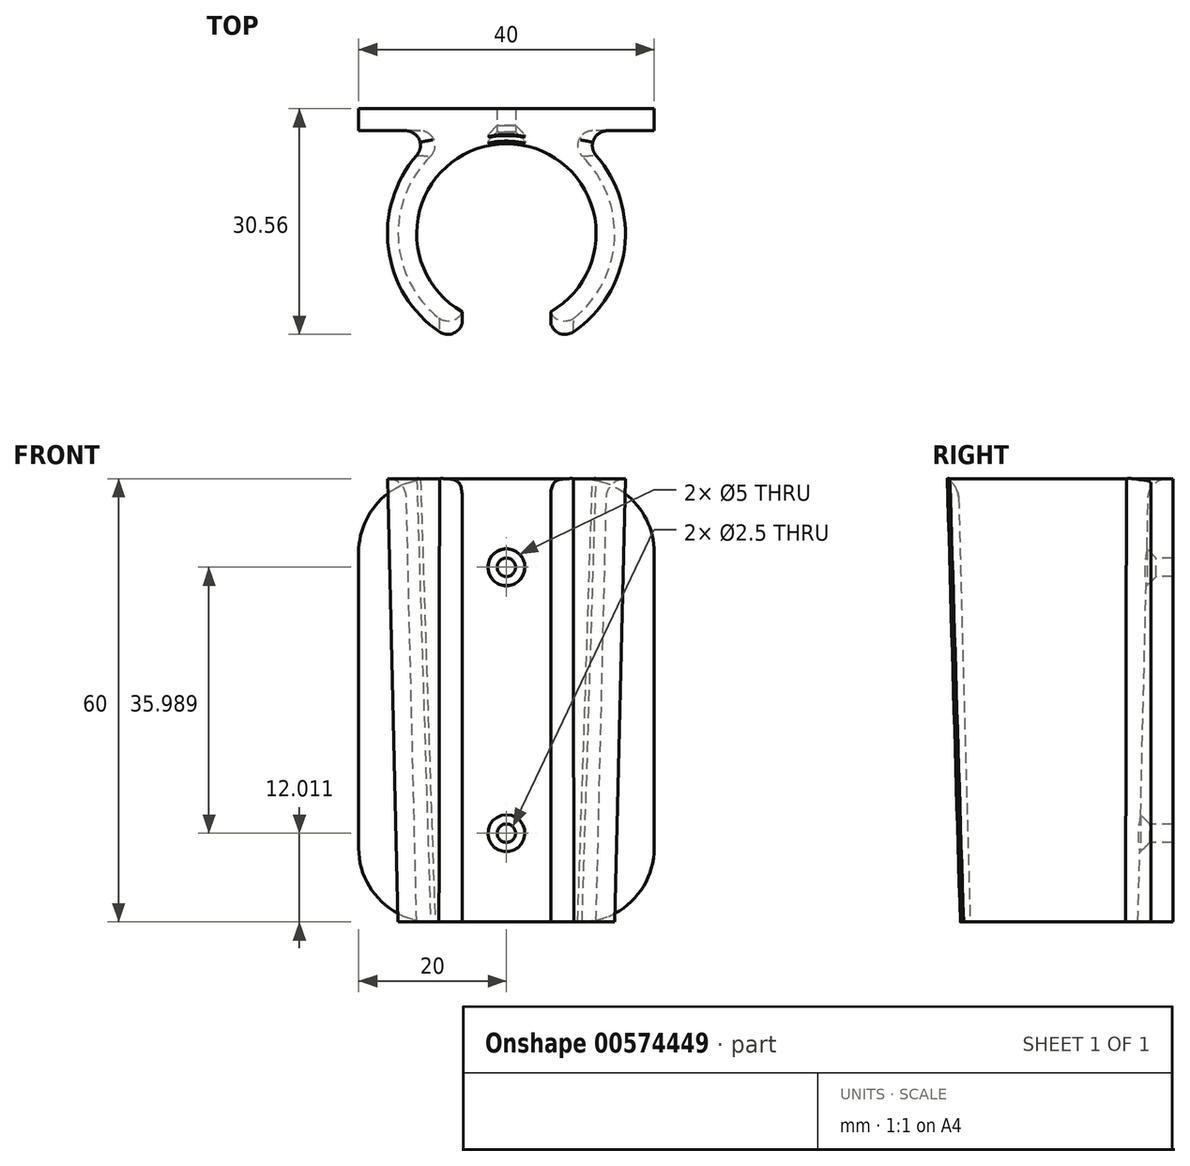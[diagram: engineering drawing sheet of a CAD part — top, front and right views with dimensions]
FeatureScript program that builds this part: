
annotation { "Feature Type Name" : "Feature", "Feature Type Description" : "" }
export const myFeature = defineFeature(function(context is Context, id is Id, definition is map)
    precondition{}
    {
        {
            var Q0;
            Q0=qCreatedBy(makeId("Top.planeOp"),FACE);
            cPlane(context, id + "F0", {"entities" : qUnion([Q0]), "cplaneType" : CPlaneType.OFFSET, "offset" : 60 * mm, "oppositeDirection" : true, "width" : 150 * mm, "height" : 150 * mm});
        }
        {
            var Q0;
            Q0=qCreatedBy(id+"F0.planeOp",FACE);
            var sketch = newSketch(context, id + "F1", { "sketchPlane" : qUnion([Q0])});
            skCircle(sketch, "E0", {"center": v(0, 0) * mm, "radius": 14.65 * mm});
            skSolve(sketch);
        }
        {
            var Q0;
            Q0=qCreatedBy(makeId("Top.planeOp"),FACE);
            var sketch = newSketch(context, id + "F2", { "sketchPlane" : qUnion([Q0])});
            skCircle(sketch, "E1", {"center": v(0, 0) * mm, "radius": 16.1 * mm});
            skSolve(sketch);
        }
        {
            var Q0;
            Q0=makeQuery(id+"F2.imprint","IMPRINT",FACE,{"disambiguationData":[TD([[makeQuery(id+"F2.imprint","IMPRINT",EDGE,{"derivedFrom":sQuery(id+"F2.wireOp",EDGE,"E1")}),1.0]])]});
            var Q1;
            Q1 = qSketchRegion(id + "F1", true);
            loft(context, id + "F3", {"sheetProfilesArray" : [{ "sheetProfileEntities" : qUnion([Q0]) }, { "sheetProfileEntities" : qUnion([Q1]) }]});
        }
        {
            var Q0;
            Q0=makeQuery(id+"F3.opLoft","CAP_FACE",FACE,{"disambiguationData":[OSD([makeQuery(id+"F2.imprint","IMPRINT",FACE,{"disambiguationData":[TD([[makeQuery(id+"F2.imprint","IMPRINT",EDGE,{"derivedFrom":sQuery(id+"F2.wireOp",EDGE,"E1")}),1.0]])]})])],"isStart":true});
            var Q1;
            Q1=makeQuery(id+"F3.opLoft","CAP_FACE",FACE,{"disambiguationData":[OSD([makeQuery(id+"F1.imprint","IMPRINT",FACE,{"disambiguationData":[TD([[makeQuery(id+"F1.imprint","IMPRINT",EDGE,{"derivedFrom":sQuery(id+"F1.wireOp",EDGE,"E0")}),1.0]])]})])],"isStart":true});
            shell(context, id + "F4", {"entities" : qUnion([Q0, Q1]), "thickness" : 2.5 * mm});
        }
        {
            var Q0;
            Q0=qCreatedBy(makeId("Front.planeOp"),FACE);
            var sketch = newSketch(context, id + "F5", { "sketchPlane" : qUnion([Q0])});
            skLineSegment(sketch, "E2", {"start": v(0, 0) * mm, "end": v(0, -60) * mm, "construction": true});
            skLineSegment(sketch, "E3", {"start": v(0, -30) * mm, "end": v(-24.5, -30) * mm, "construction": true});
            skLineSegment(sketch, "E4", {"start": v(-24.5, -30) * mm, "end": v(24.17, -30) * mm, "construction": true});
            skLineSegment(sketch, "E5.bottom", {"start": v(-6, -60) * mm, "end": v(6, -60) * mm});
            skLineSegment(sketch, "E5.top", {"start": v(-6, 0) * mm, "end": v(6, 0) * mm});
            skLineSegment(sketch, "E5.left", {"start": v(-6, -60) * mm, "end": v(-6, 0) * mm});
            skLineSegment(sketch, "E5.right", {"start": v(6, -60) * mm, "end": v(6, 0) * mm});
            skPoint(sketch, "E5.middle", {"position": v(0, -30) * mm});
            skSolve(sketch);
        }
        {
            var Q0;
            Q0 = qSketchRegion(id + "F5", true);
            extrude(context, id + "F6", {"entities" : qUnion([Q0]), "operationType" : NewBodyOperationType.REMOVE, "depth" : 48.95 * mm, "offsetDistance" : 25 * mm});
        }
        {
            var Q0;
            Q0=makeQuery(id+"F6.boolean.opBoolean","INTERSECT",EDGE,{"derivedFrom":[makeQuery(id+"F3.opLoft","SWEPT_FACE",FACE,{"disambiguationData":[OSD([sQuery(id+"F1.wireOp",EDGE,"E0"),sQuery(id+"F2.wireOp",EDGE,"E1")])]}),makeQuery(id+"F6.opExtrude","SWEPT_FACE",FACE,{"disambiguationData":[OSD([sQuery(id+"F5.wireOp",EDGE,"E5.left")])]})]});
            var Q1;
            Q1=makeQuery(id+"F6.boolean.opBoolean","INTERSECT",EDGE,{"derivedFrom":[makeQuery(id+"F3.opLoft","SWEPT_FACE",FACE,{"disambiguationData":[OSD([sQuery(id+"F1.wireOp",EDGE,"E0"),sQuery(id+"F2.wireOp",EDGE,"E1")])]}),makeQuery(id+"F6.opExtrude","SWEPT_FACE",FACE,{"disambiguationData":[OSD([sQuery(id+"F5.wireOp",EDGE,"E5.right")])]})]});
            fillet(context, id + "F7", {"entities" : qUnion([Q0, Q1]), "radius" : 2 * mm, "tangentPropagation" : true, "allowEdgeOverflow" : false});
        }
        {
            var Q0;
            Q0=qCreatedBy(makeId("Front.planeOp"),FACE);
            cPlane(context, id + "F8", {"entities" : qUnion([Q0]), "cplaneType" : CPlaneType.OFFSET, "offset" : 13.9 * mm, "oppositeDirection" : true, "width" : 150 * mm, "height" : 150 * mm});
        }
        {
            var Q0;
            Q0=qCreatedBy(id+"F8.planeOp",FACE);
            var sketch = newSketch(context, id + "F9", { "sketchPlane" : qUnion([Q0])});
            skLineSegment(sketch, "E6", {"start": v(0, 0) * mm, "end": v(0, -60) * mm, "construction": true});
            skLineSegment(sketch, "E7", {"start": v(0, -30) * mm, "end": v(15.93, -30) * mm, "construction": true});
            skLineSegment(sketch, "E8", {"start": v(15.93, -30) * mm, "end": v(-16.03, -30) * mm, "construction": true});
            skLineSegment(sketch, "E9.bottom", {"start": v(20, -60) * mm, "end": v(-20, -60) * mm});
            skLineSegment(sketch, "E9.top", {"start": v(20, 0) * mm, "end": v(-20, 0) * mm});
            skLineSegment(sketch, "E9.left", {"start": v(20, -60) * mm, "end": v(20, 0) * mm});
            skLineSegment(sketch, "E9.right", {"start": v(-20, -60) * mm, "end": v(-20, 0) * mm});
            skPoint(sketch, "E9.middle", {"position": v(0, -30) * mm});
            skSolve(sketch);
        }
        {
            var Q0;
            Q0 = qSketchRegion(id + "F9", true);
            extrude(context, id + "F10", {"entities" : qUnion([Q0]), "operationType" : NewBodyOperationType.ADD, "oppositeDirection" : true, "depth" : 3 * mm, "offsetDistance" : 25 * mm});
        }
        {
            var Q0;
            Q0=makeQuery(id+"F10.opExtrude","SWEPT_EDGE",EDGE,{"disambiguationData":[OSD([sQuery(id+"F9.wireOp",EDGE,"E9.top"),sQuery(id+"F9.wireOp",EDGE,"E9.left")])]});
            var Q1;
            Q1=makeQuery(id+"F10.opExtrude","SWEPT_EDGE",EDGE,{"disambiguationData":[OSD([sQuery(id+"F9.wireOp",EDGE,"E9.top"),sQuery(id+"F9.wireOp",EDGE,"E9.right")])]});
            var Q2;
            Q2=makeQuery(id+"F10.opExtrude","SWEPT_EDGE",EDGE,{"disambiguationData":[OSD([sQuery(id+"F9.wireOp",EDGE,"E9.bottom"),sQuery(id+"F9.wireOp",EDGE,"E9.left")])]});
            var Q3;
            Q3=makeQuery(id+"F10.opExtrude","SWEPT_EDGE",EDGE,{"disambiguationData":[OSD([sQuery(id+"F9.wireOp",EDGE,"E9.bottom"),sQuery(id+"F9.wireOp",EDGE,"E9.right")])]});
            fillet(context, id + "F11", {"entities" : qUnion([Q0, Q1, Q2, Q3]), "radius" : 10 * mm, "tangentPropagation" : true, "allowEdgeOverflow" : false});
        }
        {
            var Q0;
            Q0=makeQuery(id+"F4.opShell","OFFSET_EDGE",EDGE,{"disambiguationData":[OSD([sQuery(id+"F2.wireOp",EDGE,"E1")])]});
            fillet(context, id + "F12", {"entities" : qUnion([Q0]), "radius" : 2.6 * mm, "tangentPropagation" : true, "allowEdgeOverflow" : false});
        }
        {
            var Q0;
            Q0=qCreatedBy(makeId("Front.planeOp"),FACE);
            var sketch = newSketch(context, id + "F13", { "sketchPlane" : qUnion([Q0])});
            skCircle(sketch, "E10", {"center": v(0, -12) * mm, "radius": 1.6 * mm});
            skLineSegment(sketch, "E11", {"start": v(0, -59.99) * mm, "end": v(0, -47.99) * mm, "construction": true});
            skCircle(sketch, "E12", {"center": v(0, -47.99) * mm, "radius": 1.6 * mm});
            skSolve(sketch);
        }
        {
            var Q0;
            Q0=sQuery(id+"F13.wireOp",VERTEX,"E10.center");
            var Q1;
            Q1=sQuery(id+"F13.wireOp",VERTEX,"E12.center");
            var Q2;
            Q2=makeQuery(id+"F3.opLoft","SWEPT_BODY",BODY,{"disambiguationData":[OSD([makeQuery(id+"F1.imprint","IMPRINT",FACE,{"disambiguationData":[TD([[makeQuery(id+"F1.imprint","IMPRINT",EDGE,{"derivedFrom":sQuery(id+"F1.wireOp",EDGE,"E0")}),1.0]])]}),makeQuery(id+"F2.imprint","IMPRINT",FACE,{"disambiguationData":[TD([[makeQuery(id+"F2.imprint","IMPRINT",EDGE,{"derivedFrom":sQuery(id+"F2.wireOp",EDGE,"E1")}),1.0]])]})])]});
            hole(context, id + "F14", {"style" : HoleStyle.C_SINK, "endStyle" : HoleEndStyle.THROUGH, "holeDiameter" : 2.5 * mm, "cSinkDiameter" : 5 * mm, "cSinkAngle" : 90 * degree, "isTappedThrough" : true, "tappedDepth" : 12 * mm, "tapClearance" : 3, "locations" : qUnion([Q0, Q1]), "scope" : qUnion([Q2])});
        }
        {
            var Q0;
            Q0=makeQuery(id+"F10.boolean.opBoolean","INTERSECT",EDGE,{"disambiguationData":[OD(0.0)],"derivedFrom":[makeQuery(id+"F3.opLoft","SWEPT_FACE",FACE,{"disambiguationData":[OSD([sQuery(id+"F1.wireOp",EDGE,"E0"),sQuery(id+"F2.wireOp",EDGE,"E1")])]}),makeQuery(id+"F10.opExtrude","CAP_FACE",FACE,{"disambiguationData":[OSD([sQuery(id+"F9.wireOp",EDGE,"E9.bottom"),sQuery(id+"F9.wireOp",EDGE,"E9.top"),sQuery(id+"F9.wireOp",EDGE,"E9.left"),sQuery(id+"F9.wireOp",EDGE,"E9.right")])],"isStart":true})]});
            var Q1;
            Q1=makeQuery(id+"F10.boolean.opBoolean","INTERSECT",EDGE,{"disambiguationData":[OD(1.0)],"derivedFrom":[makeQuery(id+"F3.opLoft","SWEPT_FACE",FACE,{"disambiguationData":[OSD([sQuery(id+"F1.wireOp",EDGE,"E0"),sQuery(id+"F2.wireOp",EDGE,"E1")])]}),makeQuery(id+"F10.opExtrude","CAP_FACE",FACE,{"disambiguationData":[OSD([sQuery(id+"F9.wireOp",EDGE,"E9.bottom"),sQuery(id+"F9.wireOp",EDGE,"E9.top"),sQuery(id+"F9.wireOp",EDGE,"E9.left"),sQuery(id+"F9.wireOp",EDGE,"E9.right")])],"isStart":true})]});
            fillet(context, id + "F15", {"entities" : qUnion([Q0, Q1]), "radius" : 2 * mm, "tangentPropagation" : true, "allowEdgeOverflow" : false});
        }
    });
